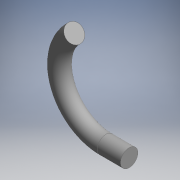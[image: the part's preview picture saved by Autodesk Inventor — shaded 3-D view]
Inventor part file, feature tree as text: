
AUTODESK INVENTOR PART (.ipt)
format: ipt  version: 2018 (Build 220112000, 112)  size: 134,144 bytes
history: native  units: in
note: dims shown in document units (in); Inventor stores cm internally (conversion verified against a paired STEP export)
features: sweep x3, extrude x1, sketch x1
ambient origin geometry x8: Origin, YZ Plane, XZ Plane, XY Plane, X Axis, Y Axis, Z Axis, Center Point
bodies: Solid1 (feature_tree)
feature tree (5):
  sweep  "Ring"
  extrude  "Extrusion2"  Depth=0.315in
  sweep  "Sweep Path"
  sweep  "Sweep Profile"
  sketch  "Sketch4"  dims[d0=0.315in d1=0.2953in d2=0.1181in d3=0.0in d4=0.0in d8=0.1575in d9=0.0in]
